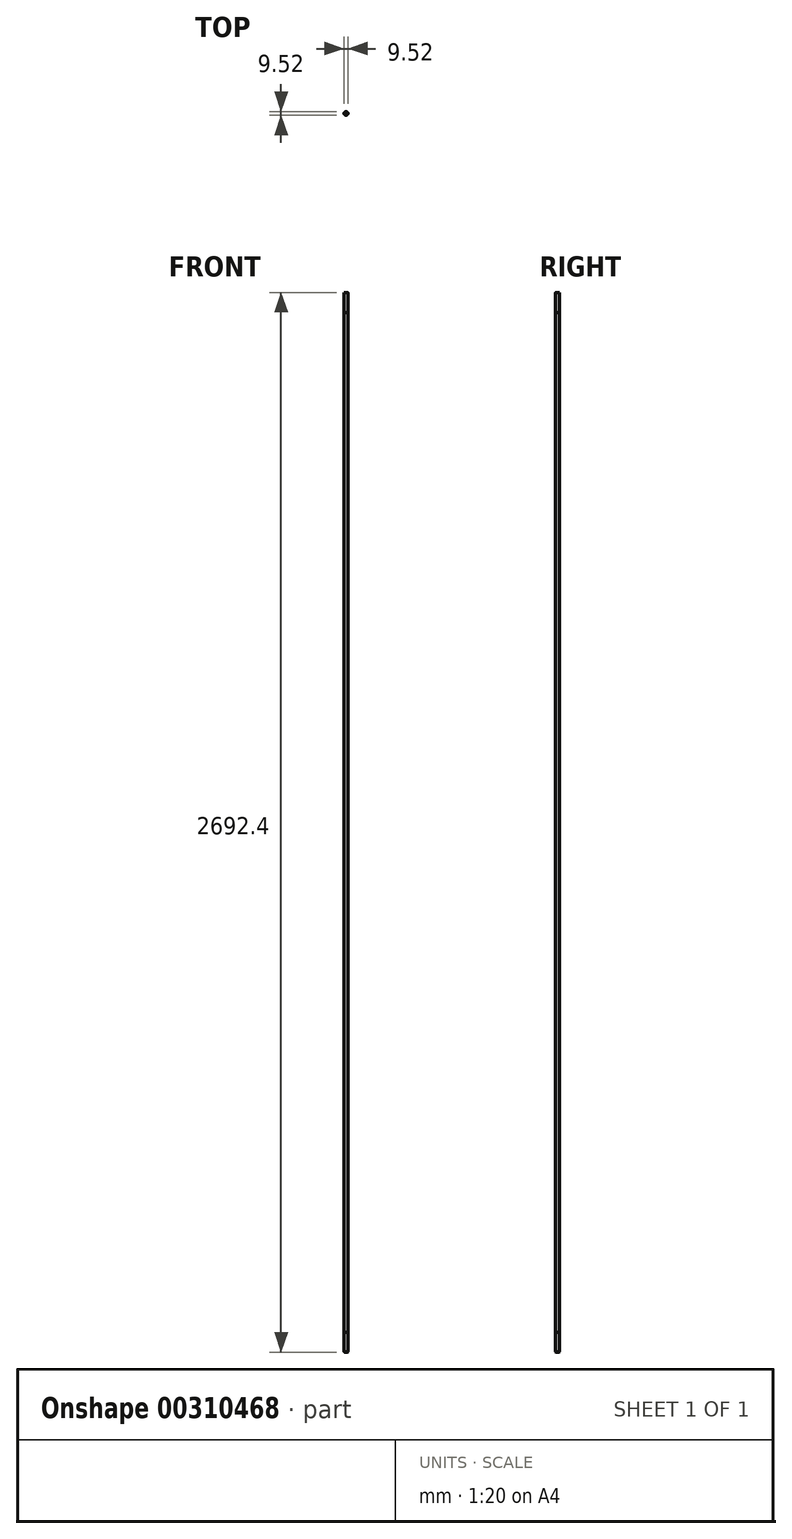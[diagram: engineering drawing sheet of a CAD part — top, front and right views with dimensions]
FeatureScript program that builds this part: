
annotation { "Feature Type Name" : "Feature", "Feature Type Description" : "" }
export const myFeature = defineFeature(function(context is Context, id is Id, definition is map)
    precondition{}
    {
        {
            var Q0;
            Q0=qCreatedBy(makeId("Top.planeOp"),FACE);
            var sketch = newSketch(context, id + "F0", { "sketchPlane" : qUnion([Q0])});
            skCircle(sketch, "E0", {"center": v(0, 0) * mm, "radius": 4.76 * mm});
            skSolve(sketch);
        }
        {
            var Q0;
            Q0=makeQuery(id+"F0.imprint","IMPRINT",FACE,{"disambiguationData":[TD([[makeQuery(id+"F0.imprint","IMPRINT",EDGE,{"derivedFrom":sQuery(id+"F0.wireOp",EDGE,"E0")}),1.0]])]});
            extrude(context, id + "F1", {"entities" : qUnion([Q0]), "endBound" : BoundingType.SYMMETRIC, "depth" : 2590.8 * mm});
        }
        {
            var Q0;
            Q0=makeQuery(id+"F1.opExtrude","CAP_FACE",FACE,{"disambiguationData":[OSD([sQuery(id+"F0.wireOp",EDGE,"E0")])],"isStart":false});
            var sketch = newSketch(context, id + "F2", { "sketchPlane" : qUnion([Q0])});
            skCircle(sketch, "E1", {"center": v(0, 0) * mm, "radius": 4.7 * mm});
            skSolve(sketch);
        }
        {
            var Q0;
            Q0=qSketchRegion(id+"F2",true);
            extrude(context, id + "F3", {"entities" : qUnion([Q0]), "depth" : 50.8 * mm});
        }
        {
            var Q0;
            Q0=makeQuery(id+"F3.opExtrude","SWEPT_BODY",BODY,{"disambiguationData":[OSD([sQuery(id+"F2.wireOp",EDGE,"E1")])]});
            var Q1;
            Q1=qCreatedBy(makeId("Top.planeOp"),FACE);
            mirror(context, id + "F4", {"operationType" : NewBodyOperationType.ADD, "entities" : qUnion([Q0]), "mirrorPlane" : qUnion([Q1])});
        }
        {
            var Q0;
            Q0=makeQuery(id+"F3.opExtrude","CAP_FACE",FACE,{"disambiguationData":[OSD([sQuery(id+"F2.wireOp",EDGE,"E1")])],"isStart":false});
            var Q1;
            Q1=makeQuery(id+"F4.opPattern","COPY",EDGE,{"derivedFrom":makeQuery(id+"F3.opExtrude","CAP_EDGE",EDGE,{"disambiguationData":[OSD([sQuery(id+"F2.wireOp",EDGE,"E1")])],"isStart":false}),"instanceName":"1"});
            chamfer(context, id + "F5", {"entities" : qUnion([Q0, Q1]), "width" : 0.76 * mm, "tangentPropagation" : true});
        }
    });
